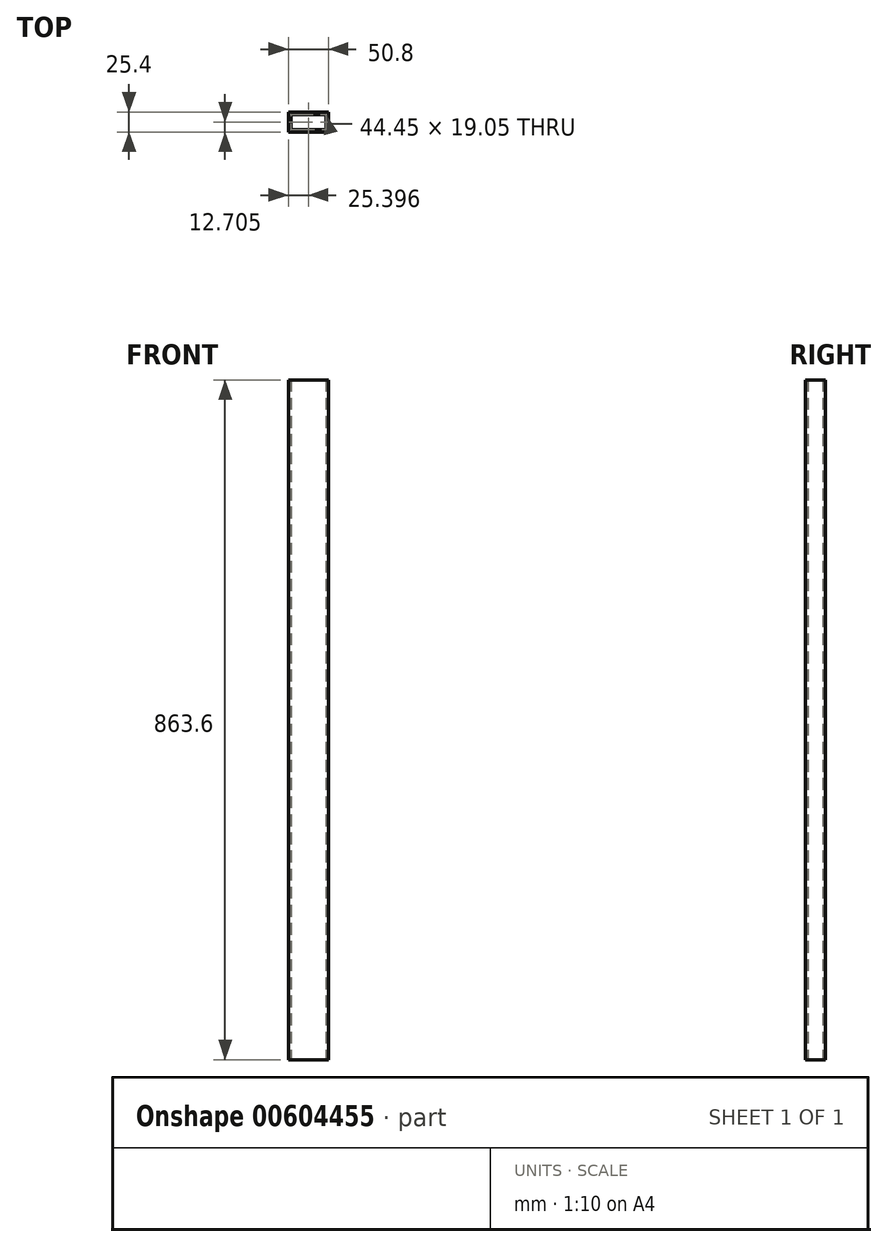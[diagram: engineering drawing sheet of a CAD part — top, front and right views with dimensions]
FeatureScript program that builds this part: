
annotation { "Feature Type Name" : "Feature", "Feature Type Description" : "" }
export const myFeature = defineFeature(function(context is Context, id is Id, definition is map)
    precondition{}
    {
        {
            var Q0;
            Q0=qCreatedBy(makeId("Top.planeOp"),FACE);
            var sketch = newSketch(context, id + "F0", { "sketchPlane" : qUnion([Q0])});
            skLineSegment(sketch, "E0.MirrorCS", {"start": v(-42.43, 26.87) * mm, "end": v(8.37, 26.87) * mm});
            skLineSegment(sketch, "E1.MirrorCS", {"start": v(-42.43, 52.27) * mm, "end": v(8.37, 52.27) * mm});
            skLineSegment(sketch, "E2.MirrorCS", {"start": v(-42.43, 26.87) * mm, "end": v(-42.43, 52.27) * mm});
            skLineSegment(sketch, "E3.MirrorCS", {"start": v(8.37, 26.87) * mm, "end": v(8.37, 52.27) * mm});
            skLineSegment(sketch, "E4.MirrorCS", {"start": v(5.2, 49.1) * mm, "end": v(5.2, 30.05) * mm});
            skLineSegment(sketch, "E5.MirrorCS", {"start": v(-39.26, 49.1) * mm, "end": v(-39.26, 30.05) * mm});
            skLineSegment(sketch, "E6.MirrorCS", {"start": v(5.2, 49.1) * mm, "end": v(-39.26, 49.1) * mm});
            skLineSegment(sketch, "E7.MirrorCS", {"start": v(5.2, 30.05) * mm, "end": v(-39.26, 30.05) * mm});
            skSolve(sketch);
        }
        {
            var Q0;
            Q0 = qSketchRegion(id + "F0", true);
            var Q1;
            Q1=makeQuery(id+"F0.imprint","IMPRINT",FACE,{"disambiguationData":[TD([[makeQuery(id+"F0.imprint","IMPRINT",EDGE,{"derivedFrom":sQuery(id+"F0.wireOp",EDGE,"E0.MirrorCS")}),1.0]])]});
            extrude(context, id + "F1", {"entities" : qUnion([Q0, Q1]), "depth" : 863.6 * mm, "offsetDistance" : 25.4 * mm});
        }
    });
